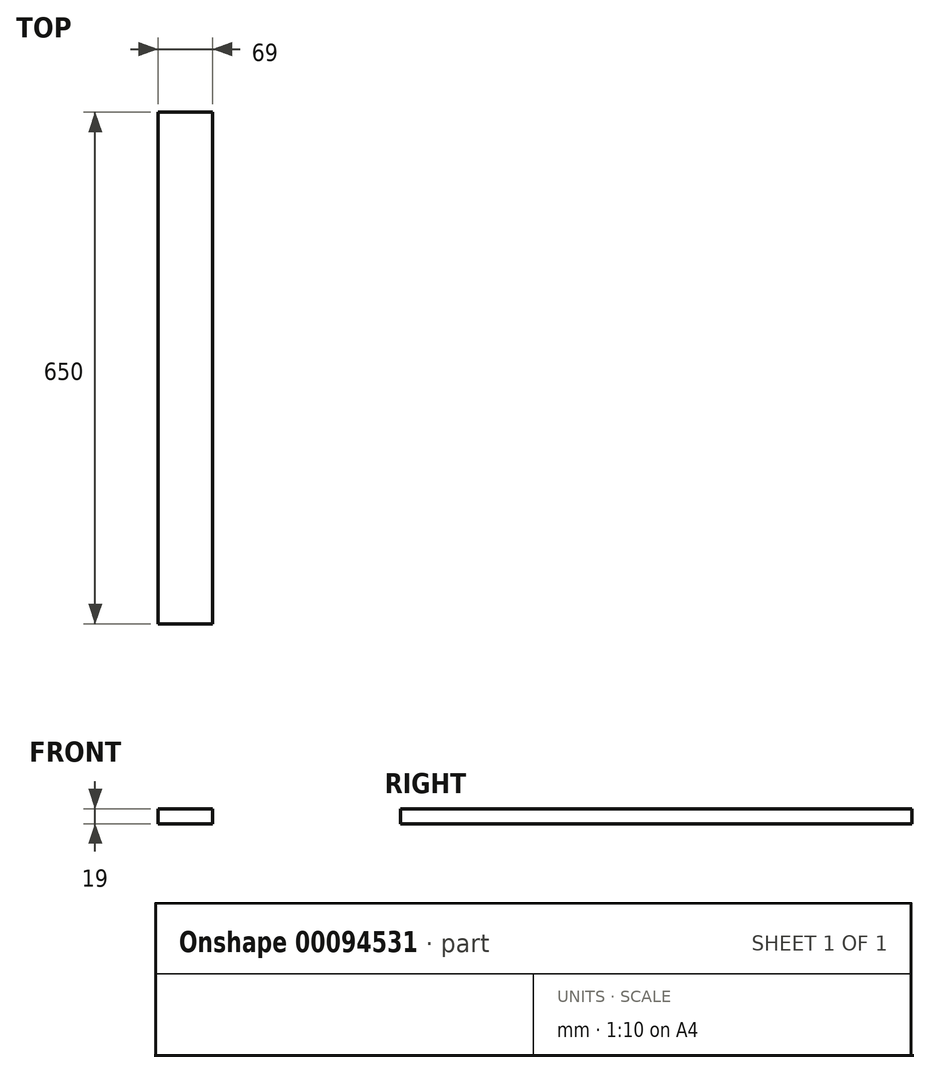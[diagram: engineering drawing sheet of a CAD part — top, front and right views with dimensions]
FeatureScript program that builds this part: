
annotation { "Feature Type Name" : "Feature", "Feature Type Description" : "" }
export const myFeature = defineFeature(function(context is Context, id is Id, definition is map)
    precondition{}
    {
        {
            var Q0;
            Q0=qCreatedBy(makeId("Top.planeOp"),FACE);
            var sketch = newSketch(context, id + "F0", { "sketchPlane" : qUnion([Q0])});
            skLineSegment(sketch, "E0.bottom", {"start": v(34.5, 325) * mm, "end": v(-34.5, 325) * mm});
            skLineSegment(sketch, "E0.top", {"start": v(34.5, -325) * mm, "end": v(-34.5, -325) * mm});
            skLineSegment(sketch, "E0.left", {"start": v(34.5, 325) * mm, "end": v(34.5, -325) * mm});
            skLineSegment(sketch, "E0.right", {"start": v(-34.5, 325) * mm, "end": v(-34.5, -325) * mm});
            skPoint(sketch, "E0.middle", {"position": v(0, 0) * mm});
            skLineSegment(sketch, "E1", {"start": v(0, 325) * mm, "end": v(0, -325) * mm, "construction": true});
            skSolve(sketch);
        }
        {
            var Q0;
            Q0 = qSketchRegion(id + "F0", true);
            extrude(context, id + "F1", {"entities" : qUnion([Q0]), "depth" : 19 * mm});
        }
    });
